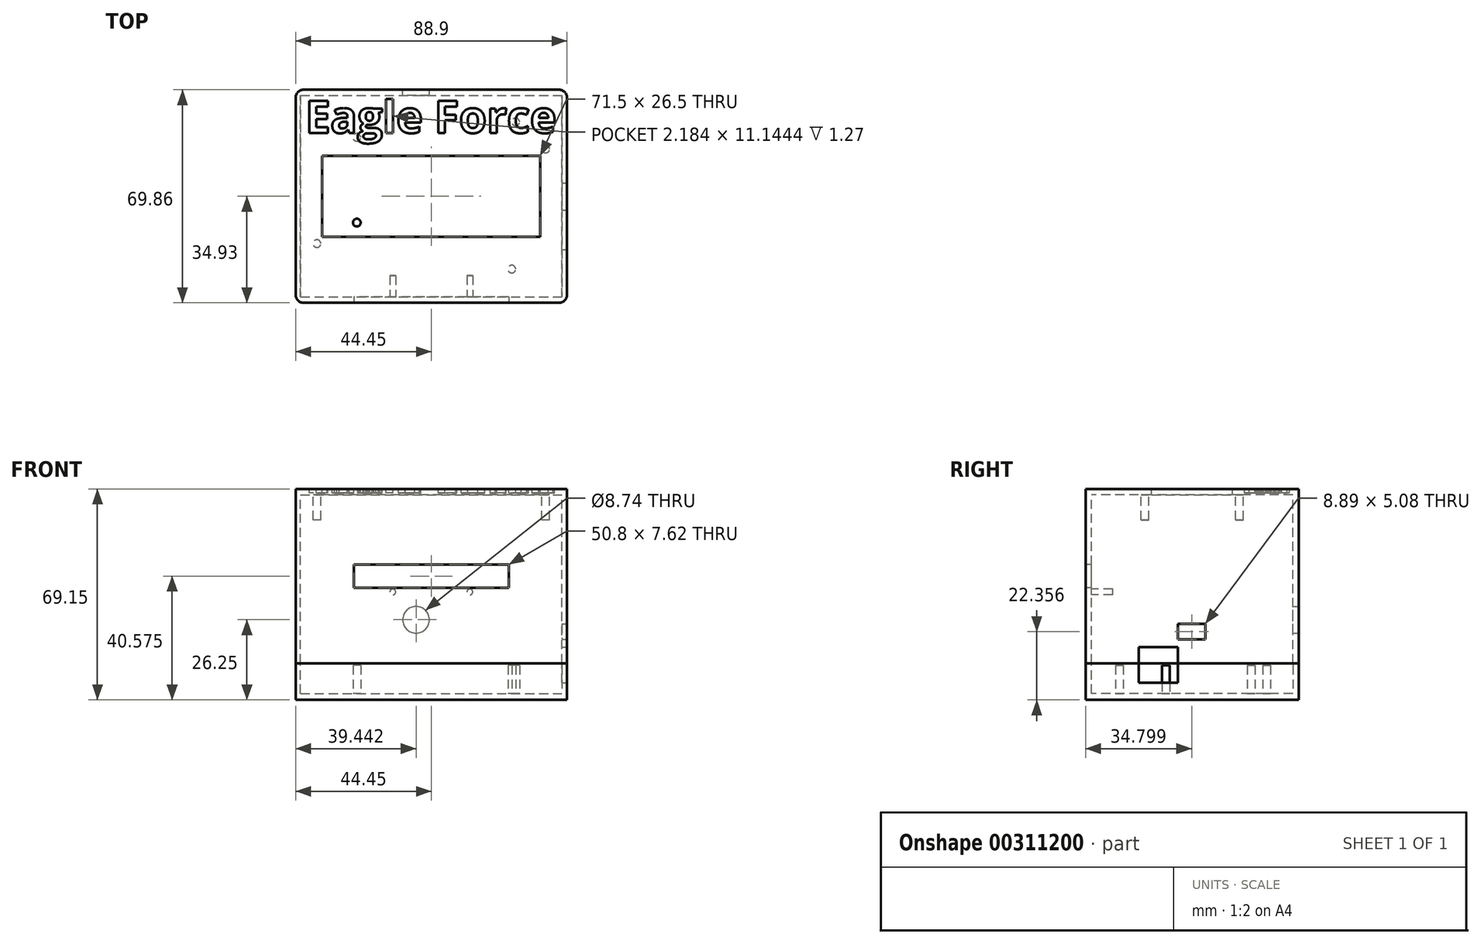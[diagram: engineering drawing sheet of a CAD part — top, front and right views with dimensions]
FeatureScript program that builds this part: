
annotation { "Feature Type Name" : "Feature", "Feature Type Description" : "" }
export const myFeature = defineFeature(function(context is Context, id is Id, definition is map)
    precondition{}
    {
        {
            var Q0;
            Q0=qCreatedBy(makeId("Top.planeOp"),FACE);
            var sketch = newSketch(context, id + "F0", { "sketchPlane" : qUnion([Q0])});
            skLineSegment(sketch, "E0.bottom", {"start": v(-44.45, 34.93) * mm, "end": v(44.45, 34.93) * mm});
            skLineSegment(sketch, "E0.top", {"start": v(-44.45, -34.93) * mm, "end": v(44.45, -34.93) * mm});
            skLineSegment(sketch, "E0.left", {"start": v(-44.45, 34.93) * mm, "end": v(-44.45, -34.93) * mm});
            skLineSegment(sketch, "E0.right", {"start": v(44.45, 34.93) * mm, "end": v(44.45, -34.93) * mm});
            skPoint(sketch, "E0.middle", {"position": v(0, 0) * mm});
            skSolve(sketch);
        }
        {
            var Q0;
            Q0 = qSketchRegion(id + "F0", true);
            extrude(context, id + "F1", {"entities" : qUnion([Q0]), "depth" : 10 * mm, "hasSecondDirection" : true, "secondDirectionOppositeDirection" : true, "secondDirectionDepth" : 2 * mm});
        }
        {
            var Q0;
            Q0=makeQuery(id+"F1.opExtrude","CAP_FACE",FACE,{"disambiguationData":[OSD([sQuery(id+"F0.wireOp",EDGE,"E0.bottom"),sQuery(id+"F0.wireOp",EDGE,"E0.top"),sQuery(id+"F0.wireOp",EDGE,"E0.left"),sQuery(id+"F0.wireOp",EDGE,"E0.right")])],"isStart":false});
            var sketch = newSketch(context, id + "F2", { "sketchPlane" : qUnion([Q0])});
            skLineSegment(sketch, "E1.bottom", {"start": v(-42.86, 33.02) * mm, "end": v(42.86, 33.02) * mm});
            skLineSegment(sketch, "E1.top", {"start": v(-42.86, -33.02) * mm, "end": v(42.86, -33.02) * mm});
            skLineSegment(sketch, "E1.left", {"start": v(-42.86, 33.02) * mm, "end": v(-42.86, -33.02) * mm});
            skLineSegment(sketch, "E1.right", {"start": v(42.86, 33.02) * mm, "end": v(42.86, -33.02) * mm});
            skPoint(sketch, "E1.middle", {"position": v(0, 0) * mm});
            skSolve(sketch);
        }
        {
            var Q0;
            Q0 = qSketchRegion(id + "F2", true);
            extrude(context, id + "F3", {"entities" : qUnion([Q0]), "operationType" : NewBodyOperationType.REMOVE, "oppositeDirection" : true, "depth" : 8.9 * mm});
        }
        {
            var Q0;
            Q0=makeQuery(id+"F1.opExtrude","SWEPT_EDGE",EDGE,{"disambiguationData":[OSD([sQuery(id+"F0.wireOp",EDGE,"E0.bottom"),sQuery(id+"F0.wireOp",EDGE,"E0.right")])]});
            var Q1;
            Q1=makeQuery(id+"F1.opExtrude","SWEPT_EDGE",EDGE,{"disambiguationData":[OSD([sQuery(id+"F0.wireOp",EDGE,"E0.top"),sQuery(id+"F0.wireOp",EDGE,"E0.right")])]});
            var Q2;
            Q2=makeQuery(id+"F1.opExtrude","SWEPT_EDGE",EDGE,{"disambiguationData":[OSD([sQuery(id+"F0.wireOp",EDGE,"E0.top"),sQuery(id+"F0.wireOp",EDGE,"E0.left")])]});
            var Q3;
            Q3=makeQuery(id+"F1.opExtrude","SWEPT_EDGE",EDGE,{"disambiguationData":[OSD([sQuery(id+"F0.wireOp",EDGE,"E0.bottom"),sQuery(id+"F0.wireOp",EDGE,"E0.left")])]});
            fillet(context, id + "F4", {"entities" : qUnion([Q0, Q1, Q2, Q3]), "radius" : 2.54 * mm, "tangentPropagation" : true, "allowEdgeOverflow" : false});
        }
        {
            var Q0;
            Q0=makeQuery(id+"F0.imprint","IMPRINT",FACE,{"disambiguationData":[TD([[makeQuery(id+"F0.imprint","IMPRINT",EDGE,{"derivedFrom":sQuery(id+"F0.wireOp",EDGE,"E0.bottom")}),-1.0]])]});
            var sketch = newSketch(context, id + "F5", { "sketchPlane" : qUnion([Q0])});
            skSolve(sketch);
        }
        {
            var Q0;
            Q0=makeQuery(id+"F5.imprint","IMPRINT",FACE,{"disambiguationData":[TD([[makeQuery(id+"F5.imprint","IMPRINT",EDGE,{"derivedFrom":makeQuery(id+"F0.imprint","IMPRINT",EDGE,{"derivedFrom":sQuery(id+"F0.wireOp",EDGE,"E0.bottom")})}),-1.0]])]});
            var sketch = newSketch(context, id + "F6", { "sketchPlane" : qUnion([Q0])});
            skLineSegment(sketch, "E2", {"start": v(42.86, 33.02) * mm, "end": v(27.65, 33.02) * mm});
            skLineSegment(sketch, "E3", {"start": v(27.65, 33.02) * mm, "end": v(27.65, 24.38) * mm});
            skLineSegment(sketch, "E4", {"start": v(27.65, 24.38) * mm, "end": v(26.38, 24.38) * mm});
            skLineSegment(sketch, "E5", {"start": v(26.38, 24.38) * mm, "end": v(26.38, -23.88) * mm});
            skCircle(sketch, "E6", {"center": v(27.65, 24.38) * mm, "radius": 1.27 * mm});
            skCircle(sketch, "E7", {"center": v(26.38, -23.88) * mm, "radius": 1.27 * mm});
            skLineSegment(sketch, "E8", {"start": v(26.38, -23.88) * mm, "end": v(-24.42, -23.88) * mm});
            skLineSegment(sketch, "E9", {"start": v(-24.42, -23.88) * mm, "end": v(-24.42, -8.64) * mm});
            skLineSegment(sketch, "E10", {"start": v(-24.42, -8.64) * mm, "end": v(-24.42, 19.3) * mm});
            skCircle(sketch, "E11", {"center": v(-24.42, -8.64) * mm, "radius": 1.27 * mm});
            skCircle(sketch, "E12", {"center": v(-24.42, 19.3) * mm, "radius": 1.27 * mm});
            skSolve(sketch);
        }
        {
            var Q0;
            Q0=makeQuery(id+"F2.imprint","IMPRINT",FACE,{"disambiguationData":[TD([[makeQuery(id+"F2.imprint","IMPRINT",EDGE,{"derivedFrom":sQuery(id+"F2.wireOp",EDGE,"E1.bottom")}),-1.0]])]});
            extrude(context, id + "F7", {"entities" : qUnion([Q0]), "operationType" : NewBodyOperationType.REMOVE, "oppositeDirection" : true, "depth" : 9.96 * mm});
        }
        {
            var Q0;
            Q0 = qSketchRegion(id + "F6", true);
            extrude(context, id + "F8", {"entities" : qUnion([Q0]), "operationType" : NewBodyOperationType.ADD, "depth" : 15.24 * mm});
        }
        {
            var Q0;
            Q0=makeQuery(id+"F1.opExtrude","SWEPT_FACE",FACE,{"disambiguationData":[OSD([sQuery(id+"F0.wireOp",EDGE,"E0.right")])]});
            var sketch = newSketch(context, id + "F9", { "sketchPlane" : qUnion([Q0])});
            skLineSegment(sketch, "E13.bottom", {"start": v(-17.53, 15.24) * mm, "end": v(-4.58, 15.24) * mm});
            skLineSegment(sketch, "E13.top", {"start": v(-17.53, 0) * mm, "end": v(-4.58, 0) * mm});
            skLineSegment(sketch, "E13.left", {"start": v(-17.53, 15.24) * mm, "end": v(-17.53, 0) * mm});
            skLineSegment(sketch, "E13.right", {"start": v(-4.58, 15.24) * mm, "end": v(-4.58, 0) * mm});
            skLineSegment(sketch, "E14", {"start": v(-17.53, 0) * mm, "end": v(-17.53, 3.63) * mm});
            skLineSegment(sketch, "E15", {"start": v(-17.53, 3.63) * mm, "end": v(-4.58, 3.63) * mm});
            skLineSegment(sketch, "E16", {"start": v(-4.58, 3.63) * mm, "end": v(-4.58, 0) * mm});
            skLineSegment(sketch, "E17", {"start": v(-17.53, 3.63) * mm, "end": v(-17.53, 0) * mm});
            skSolve(sketch);
        }
        {
            var Q0;
            Q0=makeQuery(id+"F2.imprint","IMPRINT",FACE,{"disambiguationData":[TD([[makeQuery(id+"F2.imprint","IMPRINT",EDGE,{"derivedFrom":sQuery(id+"F2.wireOp",EDGE,"E1.bottom")}),-1.0]])]});
            var sketch = newSketch(context, id + "F10", { "sketchPlane" : qUnion([Q0])});
            skLineSegment(sketch, "E18.bottom", {"start": v(-44.45, 34.93) * mm, "end": v(44.45, 34.93) * mm});
            skLineSegment(sketch, "E18.top", {"start": v(-44.45, -34.93) * mm, "end": v(44.45, -34.93) * mm});
            skLineSegment(sketch, "E18.left", {"start": v(-44.45, 34.93) * mm, "end": v(-44.45, -34.93) * mm});
            skLineSegment(sketch, "E18.right", {"start": v(44.45, 34.93) * mm, "end": v(44.45, -34.93) * mm});
            skPoint(sketch, "E18.middle", {"position": v(0, 0) * mm});
            skSolve(sketch);
        }
        {
            var Q0;
            Q0 = qSketchRegion(id + "F10", true);
            extrude(context, id + "F11", {"entities" : qUnion([Q0]), "depth" : 57.15 * mm});
        }
        {
            var Q0;
            Q0=makeQuery(id+"F11.opExtrude","CAP_FACE",FACE,{"disambiguationData":[OSD([sQuery(id+"F10.wireOp",EDGE,"E18.bottom"),sQuery(id+"F10.wireOp",EDGE,"E18.top"),sQuery(id+"F10.wireOp",EDGE,"E18.left"),sQuery(id+"F10.wireOp",EDGE,"E18.right")])],"isStart":false});
            cPlane(context, id + "F12", {"entities" : qUnion([Q0]), "cplaneType" : CPlaneType.OFFSET, "offset" : 2 * mm, "oppositeDirection" : true, "width" : 152.4 * mm, "height" : 152.4 * mm});
        }
        {
            var Q0;
            Q0=makeQuery(id+"F1.opExtrude","SWEPT_FACE",FACE,{"disambiguationData":[OSD([sQuery(id+"F0.wireOp",EDGE,"E0.right")])]});
            var sketch = newSketch(context, id + "F13", { "sketchPlane" : qUnion([Q0])});
            skLineSegment(sketch, "E19.bottom", {"start": v(-17.53, 10) * mm, "end": v(-4.58, 10) * mm});
            skLineSegment(sketch, "E19.top", {"start": v(-17.53, 15.25) * mm, "end": v(-4.58, 15.25) * mm});
            skLineSegment(sketch, "E19.left", {"start": v(-17.53, 10) * mm, "end": v(-17.53, 15.25) * mm});
            skLineSegment(sketch, "E19.right", {"start": v(-4.58, 10) * mm, "end": v(-4.58, 15.25) * mm});
            skSolve(sketch);
        }
        {
            var Q0;
            Q0 = qSketchRegion(id + "F13", true);
            extrude(context, id + "F14", {"entities" : qUnion([Q0]), "operationType" : NewBodyOperationType.REMOVE, "oppositeDirection" : true, "depth" : 3.02 * mm});
        }
        {
            var Q0;
            Q0=qCreatedBy(id+"F12.planeOp",FACE);
            var sketch = newSketch(context, id + "F15", { "sketchPlane" : qUnion([Q0])});
            skLineSegment(sketch, "E20.bottom", {"start": v(-42.86, 33.02) * mm, "end": v(42.86, 33.02) * mm});
            skLineSegment(sketch, "E20.top", {"start": v(-42.86, -33.02) * mm, "end": v(42.86, -33.02) * mm});
            skLineSegment(sketch, "E20.left", {"start": v(-42.86, 33.02) * mm, "end": v(-42.86, -33.02) * mm});
            skLineSegment(sketch, "E20.right", {"start": v(42.86, 33.02) * mm, "end": v(42.86, -33.02) * mm});
            skPoint(sketch, "E20.middle", {"position": v(0, 0) * mm});
            skSolve(sketch);
        }
        {
            var Q0;
            Q0 = qSketchRegion(id + "F15", true);
            extrude(context, id + "F16", {"entities" : qUnion([Q0]), "operationType" : NewBodyOperationType.REMOVE, "oppositeDirection" : true, "depth" : 55.88 * mm});
        }
        {
            var Q0;
            Q0=makeQuery(id+"F11.opExtrude","SWEPT_EDGE",EDGE,{"disambiguationData":[OSD([sQuery(id+"F10.wireOp",EDGE,"E18.top"),sQuery(id+"F10.wireOp",EDGE,"E18.right")])]});
            var Q1;
            Q1=makeQuery(id+"F11.opExtrude","SWEPT_EDGE",EDGE,{"disambiguationData":[OSD([sQuery(id+"F10.wireOp",EDGE,"E18.top"),sQuery(id+"F10.wireOp",EDGE,"E18.left")])]});
            var Q2;
            Q2=makeQuery(id+"F11.opExtrude","SWEPT_EDGE",EDGE,{"disambiguationData":[OSD([sQuery(id+"F10.wireOp",EDGE,"E18.bottom"),sQuery(id+"F10.wireOp",EDGE,"E18.left")])]});
            var Q3;
            Q3=makeQuery(id+"F11.opExtrude","SWEPT_EDGE",EDGE,{"disambiguationData":[OSD([sQuery(id+"F10.wireOp",EDGE,"E18.bottom"),sQuery(id+"F10.wireOp",EDGE,"E18.right")])]});
            fillet(context, id + "F17", {"entities" : qUnion([Q0, Q1, Q2, Q3]), "radius" : 2.54 * mm, "tangentPropagation" : true, "allowEdgeOverflow" : false});
        }
        {
            var Q0;
            Q0=makeQuery(id+"F11.opExtrude","SWEPT_FACE",FACE,{"disambiguationData":[OSD([sQuery(id+"F10.wireOp",EDGE,"E18.top")])]});
            var sketch = newSketch(context, id + "F18", { "sketchPlane" : qUnion([Q0])});
            skLineSegment(sketch, "E21", {"start": v(0, 10) * mm, "end": v(0, 38.58) * mm});
            skPoint(sketch, "E21.endSnap0", {"position": v(0, 67.15) * mm});
            skLineSegment(sketch, "E22.bottom", {"start": v(25.4, 34.77) * mm, "end": v(-25.4, 34.77) * mm});
            skLineSegment(sketch, "E22.top", {"start": v(25.4, 42.39) * mm, "end": v(-25.4, 42.39) * mm});
            skLineSegment(sketch, "E22.left", {"start": v(25.4, 34.77) * mm, "end": v(25.4, 42.39) * mm});
            skLineSegment(sketch, "E22.right", {"start": v(-25.4, 34.77) * mm, "end": v(-25.4, 42.39) * mm});
            skPoint(sketch, "E22.middle", {"position": v(0, 38.58) * mm});
            skLineSegment(sketch, "E23", {"start": v(25.4, 34.77) * mm, "end": v(12.63, 34.77) * mm});
            skLineSegment(sketch, "E24", {"start": v(-25.4, 34.77) * mm, "end": v(-12.63, 34.77) * mm});
            skLineSegment(sketch, "E25", {"start": v(12.63, 34.77) * mm, "end": v(12.63, 34.77) * mm});
            skLineSegment(sketch, "E26", {"start": v(12.63, 34.77) * mm, "end": v(12.63, 33.37) * mm});
            skCircle(sketch, "E27", {"center": v(12.63, 33.37) * mm, "radius": 0.95 * mm});
            skLineSegment(sketch, "E28", {"start": v(-12.63, 34.77) * mm, "end": v(-12.63, 33.37) * mm});
            skCircle(sketch, "E29", {"center": v(-12.63, 33.37) * mm, "radius": 0.95 * mm});
            skSolve(sketch);
        }
        {
            var Q0;
            Q0=makeQuery(id+"F18.imprint","IMPRINT",FACE,{"disambiguationData":[TD([[makeQuery(id+"F18.imprint","IMPRINT",EDGE,{"derivedFrom":sQuery(id+"F18.wireOp",EDGE,"E22.top")}),1.0]])]});
            extrude(context, id + "F19", {"entities" : qUnion([Q0]), "operationType" : NewBodyOperationType.REMOVE, "oppositeDirection" : true, "depth" : 6.17 * mm});
        }
        {
            var Q0;
            Q0=makeQuery(id+"F11.opExtrude","SWEPT_FACE",FACE,{"disambiguationData":[OSD([sQuery(id+"F10.wireOp",EDGE,"E18.bottom")])]});
            var sketch = newSketch(context, id + "F20", { "sketchPlane" : qUnion([Q0])});
            skLineSegment(sketch, "E30", {"start": v(-26.45, 15.26) * mm, "end": v(-13.8, 15.26) * mm});
            skLineSegment(sketch, "E31", {"start": v(-13.8, 15.26) * mm, "end": v(-13.8, 24.25) * mm});
            skLineSegment(sketch, "E32", {"start": v(-13.8, 24.25) * mm, "end": v(5, 24.25) * mm});
            skCircle(sketch, "E33", {"center": v(5, 24.25) * mm, "radius": 4.37 * mm});
            skSolve(sketch);
        }
        {
            var Q0;
            Q0=makeQuery(id+"F11.opExtrude","SWEPT_FACE",FACE,{"disambiguationData":[OSD([sQuery(id+"F10.wireOp",EDGE,"E18.right")])]});
            var sketch = newSketch(context, id + "F21", { "sketchPlane" : qUnion([Q0])});
            skLineSegment(sketch, "E34", {"start": v(-4.58, 15.25) * mm, "end": v(-4.58, 17.82) * mm});
            skLineSegment(sketch, "E35.bottom", {"start": v(-4.58, 17.82) * mm, "end": v(4.31, 17.82) * mm});
            skLineSegment(sketch, "E35.top", {"start": v(-4.58, 22.9) * mm, "end": v(4.31, 22.9) * mm});
            skLineSegment(sketch, "E35.left", {"start": v(-4.58, 17.82) * mm, "end": v(-4.58, 22.9) * mm});
            skLineSegment(sketch, "E35.right", {"start": v(4.31, 17.82) * mm, "end": v(4.31, 22.9) * mm});
            skSolve(sketch);
        }
        {
            var Q0;
            Q0 = qSketchRegion(id + "F21", true);
            extrude(context, id + "F22", {"entities" : qUnion([Q0]), "operationType" : NewBodyOperationType.REMOVE, "oppositeDirection" : true, "depth" : 7.62 * mm});
        }
        {
            var Q0;
            Q0=makeQuery(id+"F11.opExtrude","CAP_FACE",FACE,{"disambiguationData":[OSD([sQuery(id+"F10.wireOp",EDGE,"E18.bottom"),sQuery(id+"F10.wireOp",EDGE,"E18.top"),sQuery(id+"F10.wireOp",EDGE,"E18.left"),sQuery(id+"F10.wireOp",EDGE,"E18.right")])],"isStart":false});
            var sketch = newSketch(context, id + "F23", { "sketchPlane" : qUnion([Q0])});
            skLineSegment(sketch, "E36", {"start": v(-41.9, -32.39) * mm, "end": v(0, -32.39) * mm});
            skLineSegment(sketch, "E37", {"start": v(0, -32.39) * mm, "end": v(0, 0) * mm});
            skLineSegment(sketch, "E38.bottom", {"start": v(35.75, -13.25) * mm, "end": v(-35.75, -13.25) * mm});
            skLineSegment(sketch, "E38.top", {"start": v(35.75, 13.25) * mm, "end": v(-35.75, 13.25) * mm});
            skLineSegment(sketch, "E38.left", {"start": v(35.75, -13.25) * mm, "end": v(35.75, 13.25) * mm});
            skLineSegment(sketch, "E38.right", {"start": v(-35.75, -13.25) * mm, "end": v(-35.75, 13.25) * mm});
            skPoint(sketch, "E38.middle", {"position": v(0, 0) * mm});
            skLineSegment(sketch, "E39.bottom", {"start": v(37.5, -15.5) * mm, "end": v(-37.5, -15.5) * mm});
            skLineSegment(sketch, "E39.top", {"start": v(37.5, 15.5) * mm, "end": v(-37.5, 15.5) * mm});
            skLineSegment(sketch, "E39.left", {"start": v(37.5, -15.5) * mm, "end": v(37.5, 15.5) * mm});
            skLineSegment(sketch, "E39.right", {"start": v(-37.5, -15.5) * mm, "end": v(-37.5, 15.5) * mm});
            skCircle(sketch, "E40", {"center": v(-37.5, -15.5) * mm, "radius": 1.27 * mm});
            skCircle(sketch, "E41", {"center": v(-37.5, 15.5) * mm, "radius": 1.27 * mm});
            skCircle(sketch, "E42", {"center": v(37.5, 15.5) * mm, "radius": 1.27 * mm});
            skCircle(sketch, "E43", {"center": v(37.5, -15.5) * mm, "radius": 1.27 * mm});
            skSolve(sketch);
        }
        {
            var Q0;
            Q0=makeQuery(id+"F23.imprint","IMPRINT",FACE,{"disambiguationData":[TD([[makeQuery(id+"F23.imprint","IMPRINT",EDGE,{"derivedFrom":sQuery(id+"F23.wireOp",EDGE,"E38.top")}),1.0]])]});
            extrude(context, id + "F24", {"entities" : qUnion([Q0]), "operationType" : NewBodyOperationType.REMOVE, "oppositeDirection" : true, "depth" : 5.08 * mm});
        }
        {
            var Q0;
            Q0=makeQuery(id+"F11.opExtrude","CAP_FACE",FACE,{"disambiguationData":[OSD([sQuery(id+"F10.wireOp",EDGE,"E18.bottom"),sQuery(id+"F10.wireOp",EDGE,"E18.top"),sQuery(id+"F10.wireOp",EDGE,"E18.left"),sQuery(id+"F10.wireOp",EDGE,"E18.right")])],"isStart":false});
            var sketch = newSketch(context, id + "F25", { "sketchPlane" : qUnion([Q0])});
            skText(sketch, "E44", { "text": "Eagle Force\n", "fontName": "OpenSans-Bold.ttf"});
            const initialGuessF25  = {"E44": [-0.0413, 0.02076, 1, 0, 0.01056]};
            skSetInitialGuess(sketch, initialGuessF25);
            skSolve(sketch);
        }
        {
            var Q0;
            Q0=makeQuery(id+"F25.imprint","IMPRINT",FACE,{"disambiguationData":[TD([[makeQuery(id+"F25.imprint","IMPRINT",EDGE,{"derivedFrom":sQuery(id+"F25.wireOp",EDGE,"E44.sketch_text.stroke-0")}),-1.0]])]});
            var Q1;
            Q1=makeQuery(id+"F25.imprint","IMPRINT",FACE,{"disambiguationData":[TD([[makeQuery(id+"F25.imprint","IMPRINT",EDGE,{"derivedFrom":sQuery(id+"F25.wireOp",EDGE,"E44.sketch_text.stroke-12")}),-1.0]])]});
            var Q2;
            Q2=makeQuery(id+"F25.imprint","IMPRINT",FACE,{"disambiguationData":[TD([[makeQuery(id+"F25.imprint","IMPRINT",EDGE,{"derivedFrom":sQuery(id+"F25.wireOp",EDGE,"E44.sketch_text.stroke-37")}),-1.0]])]});
            var Q3;
            Q3=makeQuery(id+"F25.imprint","IMPRINT",FACE,{"disambiguationData":[TD([[makeQuery(id+"F25.imprint","IMPRINT",EDGE,{"derivedFrom":sQuery(id+"F25.wireOp",EDGE,"E44.sketch_text.stroke-81")}),-1.0]])]});
            var Q4;
            Q4=makeQuery(id+"F25.imprint","IMPRINT",FACE,{"disambiguationData":[TD([[makeQuery(id+"F25.imprint","IMPRINT",EDGE,{"derivedFrom":sQuery(id+"F25.wireOp",EDGE,"E44.sketch_text.stroke-85")}),-1.0]])]});
            var Q5;
            Q5=makeQuery(id+"F25.imprint","IMPRINT",FACE,{"disambiguationData":[TD([[makeQuery(id+"F25.imprint","IMPRINT",EDGE,{"derivedFrom":sQuery(id+"F25.wireOp",EDGE,"E44.sketch_text.stroke-105")}),-1.0]])]});
            var Q6;
            Q6=makeQuery(id+"F25.imprint","IMPRINT",FACE,{"disambiguationData":[TD([[makeQuery(id+"F25.imprint","IMPRINT",EDGE,{"derivedFrom":sQuery(id+"F25.wireOp",EDGE,"E44.sketch_text.stroke-115")}),-1.0]])]});
            var Q7;
            Q7=makeQuery(id+"F25.imprint","IMPRINT",FACE,{"disambiguationData":[TD([[makeQuery(id+"F25.imprint","IMPRINT",EDGE,{"derivedFrom":sQuery(id+"F25.wireOp",EDGE,"E44.sketch_text.stroke-133")}),-1.0]])]});
            var Q8;
            Q8=makeQuery(id+"F25.imprint","IMPRINT",FACE,{"disambiguationData":[TD([[makeQuery(id+"F25.imprint","IMPRINT",EDGE,{"derivedFrom":sQuery(id+"F25.wireOp",EDGE,"E44.sketch_text.stroke-146")}),-1.0]])]});
            var Q9;
            Q9=makeQuery(id+"F25.imprint","IMPRINT",FACE,{"disambiguationData":[TD([[makeQuery(id+"F25.imprint","IMPRINT",EDGE,{"derivedFrom":sQuery(id+"F25.wireOp",EDGE,"E44.sketch_text.stroke-160")}),-1.0]])]});
            extrude(context, id + "F26", {"entities" : qUnion([Q0, Q1, Q2, Q3, Q4, Q5, Q6, Q7, Q8, Q9]), "operationType" : NewBodyOperationType.REMOVE, "oppositeDirection" : true, "depth" : 1.27 * mm});
        }
        {
            var Q0;
            Q0=makeQuery(id+"F18.imprint","IMPRINT",FACE,{"disambiguationData":[TD([[makeQuery(id+"F18.imprint","IMPRINT",EDGE,{"derivedFrom":sQuery(id+"F18.wireOp",EDGE,"E29")}),1.0]])]});
            var Q1;
            Q1=makeQuery(id+"F18.imprint","IMPRINT",FACE,{"disambiguationData":[TD([[makeQuery(id+"F18.imprint","IMPRINT",EDGE,{"derivedFrom":sQuery(id+"F18.wireOp",EDGE,"E27")}),1.0]])]});
            extrude(context, id + "F27", {"entities" : qUnion([Q0, Q1]), "operationType" : NewBodyOperationType.ADD, "oppositeDirection" : true, "depth" : 8.9 * mm});
        }
        {
            var Q0;
            Q0=makeQuery(id+"F20.imprint","IMPRINT",FACE,{"disambiguationData":[TD([[makeQuery(id+"F20.imprint","IMPRINT",EDGE,{"derivedFrom":sQuery(id+"F20.wireOp",EDGE,"E33")}),1.0]])]});
            extrude(context, id + "F28", {"entities" : qUnion([Q0]), "operationType" : NewBodyOperationType.REMOVE, "oppositeDirection" : true, "depth" : 6.1 * mm});
        }
        {
            var Q0;
            {var subQ0=sQuery(id+"F23.wireOp",EDGE,"E39.right");var subQ1=sQuery(id+"F23.wireOp",EDGE,"E39.bottom");var subQ2=makeQuery(id+"F23.imprint","INTERSECT",VERTEX,{"derivedFrom":[subQ1,subQ0]});Q0=makeQuery(id+"F23.imprint","IMPRINT",FACE,{"disambiguationData":[TD([[makeQuery(id+"F23.imprint","IMPRINT",EDGE,{"disambiguationData":[TD([[subQ2,1.0]])],"derivedFrom":subQ1}),1.0]])]});}
            var Q1;
            {var subQ0=sQuery(id+"F23.wireOp",EDGE,"E39.right");var subQ1=sQuery(id+"F23.wireOp",EDGE,"E39.bottom");var subQ2=makeQuery(id+"F23.imprint","INTERSECT",VERTEX,{"derivedFrom":[subQ1,subQ0]});Q1=makeQuery(id+"F23.imprint","IMPRINT",FACE,{"disambiguationData":[TD([[makeQuery(id+"F23.imprint","IMPRINT",EDGE,{"disambiguationData":[TD([[subQ2,1.0]])],"derivedFrom":subQ1}),-1.0]])]});}
            var Q2;
            {var subQ0=sQuery(id+"F23.wireOp",EDGE,"E39.left");var subQ1=sQuery(id+"F23.wireOp",EDGE,"E39.top");var subQ2=makeQuery(id+"F23.imprint","INTERSECT",VERTEX,{"derivedFrom":[subQ1,subQ0]});Q2=makeQuery(id+"F23.imprint","IMPRINT",FACE,{"disambiguationData":[TD([[makeQuery(id+"F23.imprint","IMPRINT",EDGE,{"disambiguationData":[TD([[subQ2,-1.0]])],"derivedFrom":subQ1}),-1.0]])]});}
            var Q3;
            {var subQ0=sQuery(id+"F23.wireOp",EDGE,"E39.left");var subQ1=sQuery(id+"F23.wireOp",EDGE,"E39.top");var subQ2=makeQuery(id+"F23.imprint","INTERSECT",VERTEX,{"derivedFrom":[subQ1,subQ0]});Q3=makeQuery(id+"F23.imprint","IMPRINT",FACE,{"disambiguationData":[TD([[makeQuery(id+"F23.imprint","IMPRINT",EDGE,{"disambiguationData":[TD([[subQ2,-1.0]])],"derivedFrom":subQ1}),1.0]])]});}
            extrude(context, id + "F29", {"entities" : qUnion([Q0, Q1, Q2, Q3]), "operationType" : NewBodyOperationType.ADD, "oppositeDirection" : true, "depth" : 10.16 * mm});
        }
        {
            var Q0;
            {var subQ0=sQuery(id+"F9.wireOp",EDGE,"E15");Q0=makeQuery(id+"F9.imprint","IMPRINT",FACE,{"disambiguationData":[TD([[makeQuery(id+"F9.imprint","IMPRINT",EDGE,{"derivedFrom":subQ0}),1.0]])]});}
            var Q1;
            {var subQ0=sQuery(id+"F9.wireOp",EDGE,"E13.bottom");Q1=makeQuery(id+"F9.imprint","IMPRINT",FACE,{"disambiguationData":[TD([[makeQuery(id+"F9.imprint","IMPRINT",EDGE,{"derivedFrom":subQ0}),-1.0]])]});}
            extrude(context, id + "F30", {"entities" : qUnion([Q0, Q1]), "operationType" : NewBodyOperationType.REMOVE, "oppositeDirection" : true, "depth" : 6.86 * mm});
        }
    });
